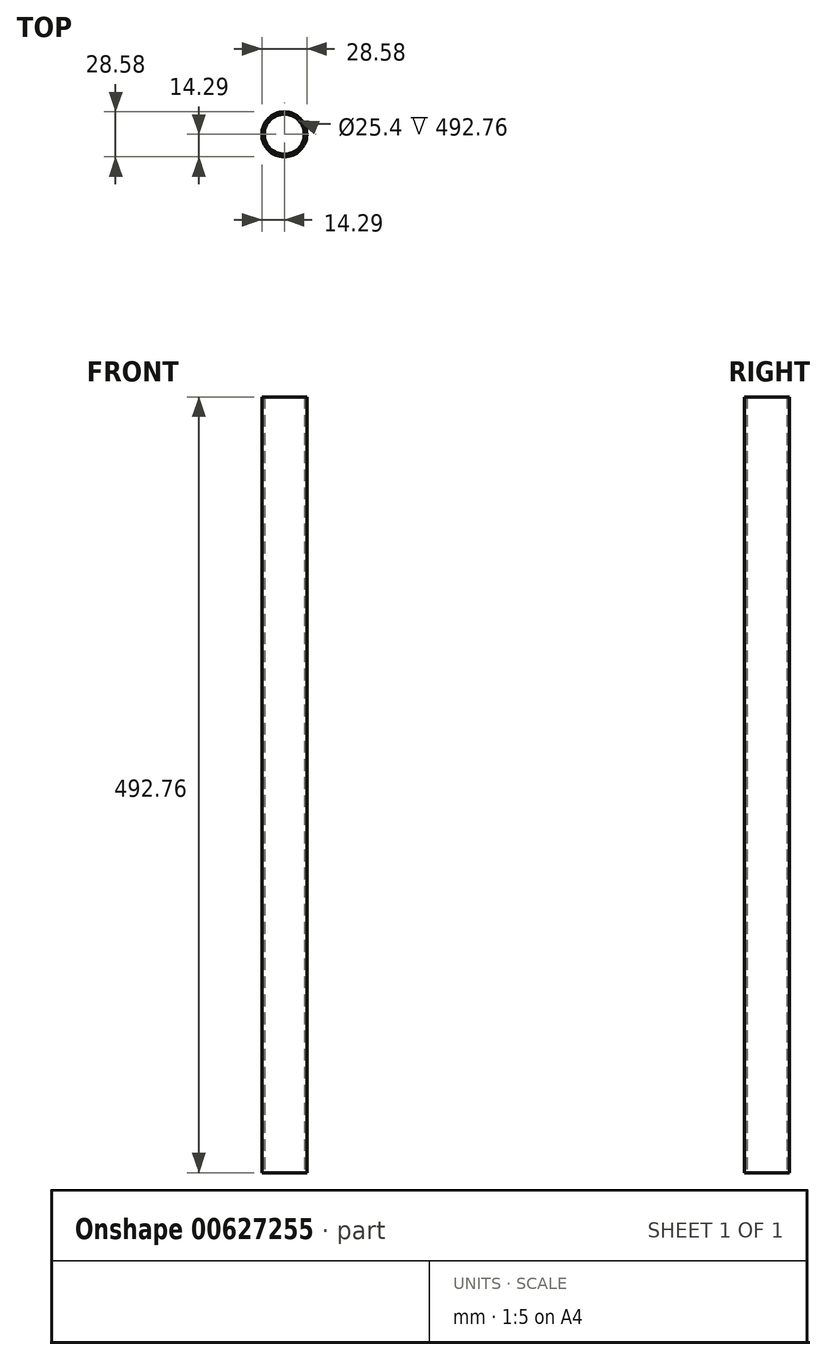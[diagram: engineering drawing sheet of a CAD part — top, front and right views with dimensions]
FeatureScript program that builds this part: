
annotation { "Feature Type Name" : "Feature", "Feature Type Description" : "" }
export const myFeature = defineFeature(function(context is Context, id is Id, definition is map)
    precondition{}
    {
        {
            var Q0;
            Q0=qCreatedBy(makeId("Top.planeOp"),FACE);
            var sketch = newSketch(context, id + "F0", { "sketchPlane" : qUnion([Q0])});
            skLineSegment(sketch, "E0", {"start": v(0, 0) * mm, "end": v(12.7, 0) * mm});
            skCircle(sketch, "E1", {"center": v(0, 0) * mm, "radius": 12.7 * mm});
            skCircle(sketch, "E2.0", {"center": v(0, 0) * mm, "radius": 14.29 * mm});
            skSolve(sketch);
        }
        {
            var Q0;
            Q0=qCreatedBy(makeId("Top.planeOp"),FACE);
            var sketch = newSketch(context, id + "F1", { "sketchPlane" : qUnion([Q0])});
            skSolve(sketch);
        }
        {
            var Q0;
            Q0=qSketchRegion(id+"F1",true);
            var Q1;
            Q1=makeQuery(id+"F0.imprint","IMPRINT",FACE,{"disambiguationData":[TD([[makeQuery(id+"F0.imprint","IMPRINT",EDGE,{"derivedFrom":sQuery(id+"F0.wireOp",EDGE,"E1")}),-1.0]])]});
            extrude(context, id + "F2", {"entities" : qUnion([Q0, Q1]), "depth" : 492.76 * mm, "offsetDistance" : 25.4 * mm});
        }
    });
